# Revit family: Hager-GAMMA-Surface_mounted-IP30-Without_Cover-With_DIN-Hosted-BE-fr
name_source: partatom
category: Electrical Equipment
units: mm (PartAtom-declared; Revit-internal decimal feet)

## family parameters
Cut with Voids When Loaded = No
Host = Face
Maintain Annotation Orientation = Yes
Panel Configuration = Two Columns, Circuits Across
Part Type = Panelboard
Room Calculation Point = No
Round Connector Dimension = Use Diameter
Shared = No

## types (4) — shared parameters
BC_MODEL_ID = 1554269
BC_OBJECT_ID = 513848
BC_OBJECT_VERSION = #5
Code hager = ADD-EC000214_EU
EF000003 - Type de montage = Apparent
EF000008 - Largeur = 250 mm  [stored 0.82021 ft]
EF000024 - Résistant aux UV = No
EF000049 - Profondeur = 103 mm  [stored 0.337927 ft]
EF000116 - Numéro RAL = 9010
EF000118 - Avec plaque de montage = No
EF001062 - Finition CEM = No
EF001088 - Possibilité de montage en saillie = No
EF001134 - Avec Rail DIN = Yes
EF002950 - Largeur dans les unités de partition = 13
EF005474 - Classe de protection (IP) = IP30
EF006244 - Couvercle/porte transparent(e) = No
EF006306 - Avec serrure = No
EF015776 - Borne de mise à la terre = No
EF015777 - Borne à conducteur neutre = No
EF015941 - Porte pour transmission du signal = Yes
ETIM class code = EC000214
ETIM class name = Small distribution board
HG000001-nombre de colonnes = 1
HG000002-avec porte = No
HG000003-Gamme = GAMMA
HG000005-Epaisseur = 2 mm  [stored 0.00656168 ft]
HG000006-Encastré = No
HG000009-Porte à double battant = No
HG000010-Portes asymétriques = No
HG000011-Rangées du bas vides = No
HG000012-Angle de pivotement de la porte = 90.00°
HG000013-Porte à gauche = No
HG000014-Porte à droite = Yes
HG000015-Visibilité de l'emprise de la porte = Yes
HG000016-Visibilité de la porte 3D = Yes
HG000017-Distance entre pôles = 18 mm  [stored 0.0590551 ft]
HG000060-RAL-number = 9010
HG000099-ID modèle Onfly = 507532
HGEF0002950-largeur en nombre de modules = 13
Manufacturer = Hager
Name = GAMMA-Surface_mounted-IP30-Without_Cover-With_DIN-BE
Name BIM&CO = Electricity
Name hager = ADD_Enclosures_EC000214
Uniformat = Low Tension Service & Dist.
Uniformat code = D501001
zero-valued in all types: Default Elevation, EF000218 - Profondeur d'encastrement, EF000332 - Hauteur d'encastrement, EF000846 - Largeur de montage, EF001131 - Profondeur intérieure, HG000007-Nombre de colonnes vides, HG000008-Nombre de rangées vides

## per-type parameters (varying)
| type | BC_VARIANT_ID | EF000040 - Hauteur | EF000266 - Nombre de rangées | HG000004-Référence fabricant | HGEF000266-Nombre de rangées |
| GAMMA-Surface_mounted_W250_H250_D103_13_Modular_Spacing-GD113U | 1178806 | 250 mm  [stored 0.82021 ft] | 1 | GD113U | 1 |
| GAMMA-Surface_mounted_W250_H375_D103_13_Modular_Spacing-GD213U | 1178807 | 375 mm  [stored 1.23031 ft] | 2 | GD213U | 2 |
| GAMMA-Surface_mounted_W250_H500_D103_13_Modular_Spacing-GD313U | 1178808 | 500 mm  [stored 1.64042 ft] | 3 | GD313U | 3 |
| GAMMA-Surface_mounted_W250_H625_D103_13_Modular_Spacing-GD413U | 1178809 | 625 mm  [stored 2.05052 ft] | 4 | GD413U | 4 |

note: column(s) folded — value = type name in every type: Reference

note: [stored X ft] marks values corroborated as IEEE doubles in the binary element streams (Revit-internal decimal feet)

## geometry (parser evidence)
native form markers: Sweep x14
no freeform markers — native parametric forms only
